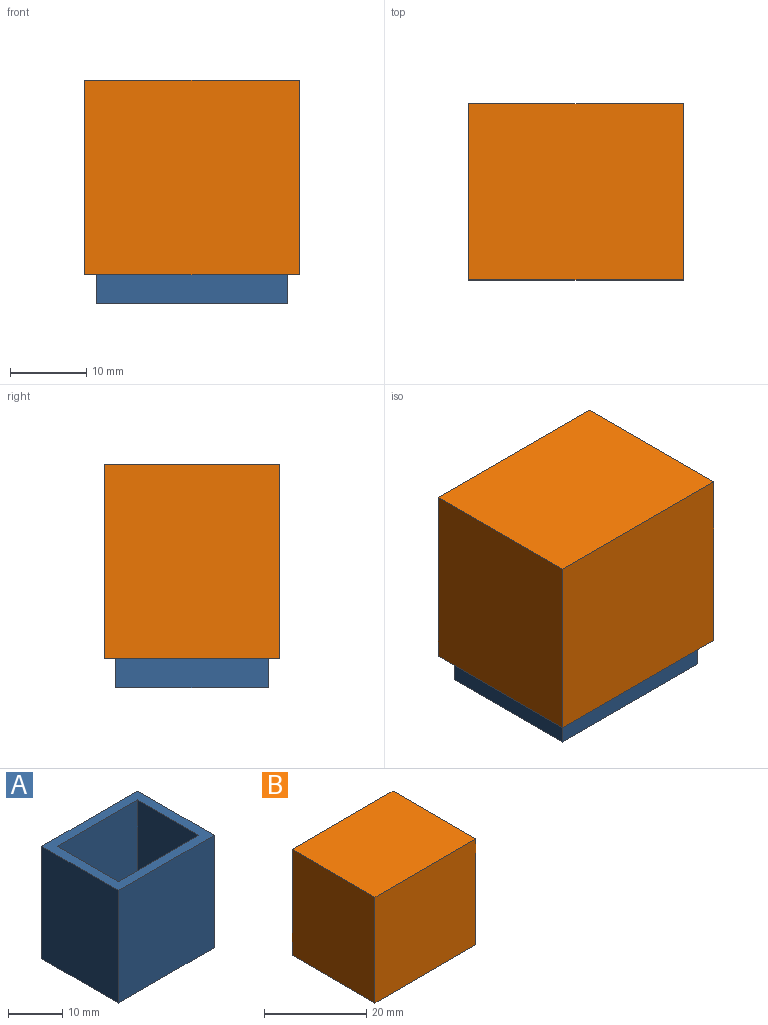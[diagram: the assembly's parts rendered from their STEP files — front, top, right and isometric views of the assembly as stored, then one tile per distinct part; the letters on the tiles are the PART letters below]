
ASSEMBLY  parts=2 mates=1
PART A: 11 faces, bbox 25x20x25.4 mm
  f0: plane 25x20mm, normal (0,0,1), area 164mm2, adj f1,f2,f3,f4,f6,f7,f8,f9
  f1: plane 25.4x20mm, normal (1,0,0), area 508mm2, adj f0,f2,f4,f5
  f2: plane 25.4x25mm, normal (0,1,0), area 635mm2, adj f0,f1,f3,f5
  f3: plane 25.4x20mm, normal (-1,0,0), area 508mm2, adj f0,f2,f4,f5
  f4: plane 25.4x25mm, normal (0,-1,0), area 635mm2, adj f0,f1,f3,f5
  f5: plane 25x20mm, normal (0,0,-1), area 500mm2, adj f1,f2,f3,f4
  f6: plane 23.4x16mm, normal (-1,0,0), area 374.4mm2, adj f0,f7,f9,f10
  f7: plane 23.4x21mm, normal (0,-1,0), area 491.4mm2, adj f0,f6,f8,f10
  f8: plane 23.4x16mm, normal (1,0,0), area 374.4mm2, adj f0,f7,f9,f10
  f9: plane 23.4x21mm, normal (0,1,0), area 491.4mm2, adj f0,f6,f8,f10
  f10: plane 21x16mm, normal (0,0,1), area 336mm2, adj f6,f7,f8,f9
PART B: 11 faces, bbox 28x23x25.4 mm
  f0: plane 28x23mm, normal (0,0,-1), area 98mm2, adj f1,f2,f3,f4,f6,f7,f8,f9
  f1: plane 25.4x23mm, normal (1,0,0), area 584.2mm2, adj f0,f2,f4,f5
  f2: plane 28x25.4mm, normal (0,1,0), area 711.2mm2, adj f0,f1,f3,f5
  f3: plane 25.4x23mm, normal (-1,0,0), area 584.2mm2, adj f0,f2,f4,f5
  f4: plane 28x25.4mm, normal (0,-1,0), area 711.2mm2, adj f0,f1,f3,f5
  f5: plane 28x23mm, normal (0,0,1), area 644mm2, adj f1,f2,f3,f4
  f6: plane 24.4x21mm, normal (-1,0,0), area 512.4mm2, adj f0,f7,f9,f10
  f7: plane 26x24.4mm, normal (0,-1,0), area 634.4mm2, adj f0,f6,f8,f10
  f8: plane 24.4x21mm, normal (1,0,0), area 512.4mm2, adj f0,f7,f9,f10
  f9: plane 26x24.4mm, normal (0,1,0), area 634.4mm2, adj f0,f6,f8,f10
  f10: plane 26x21mm, normal (0,0,-1), area 546mm2, adj f6,f7,f8,f9
PLACE A t=(23.2,5.48,-4.33)mm
PLACE B t=(23.2,5.48,-0.57)mm
MATE slider A.f10 <-> B.f10  axis (0,0,1) through (23.2,5.48,-2.33)mm
